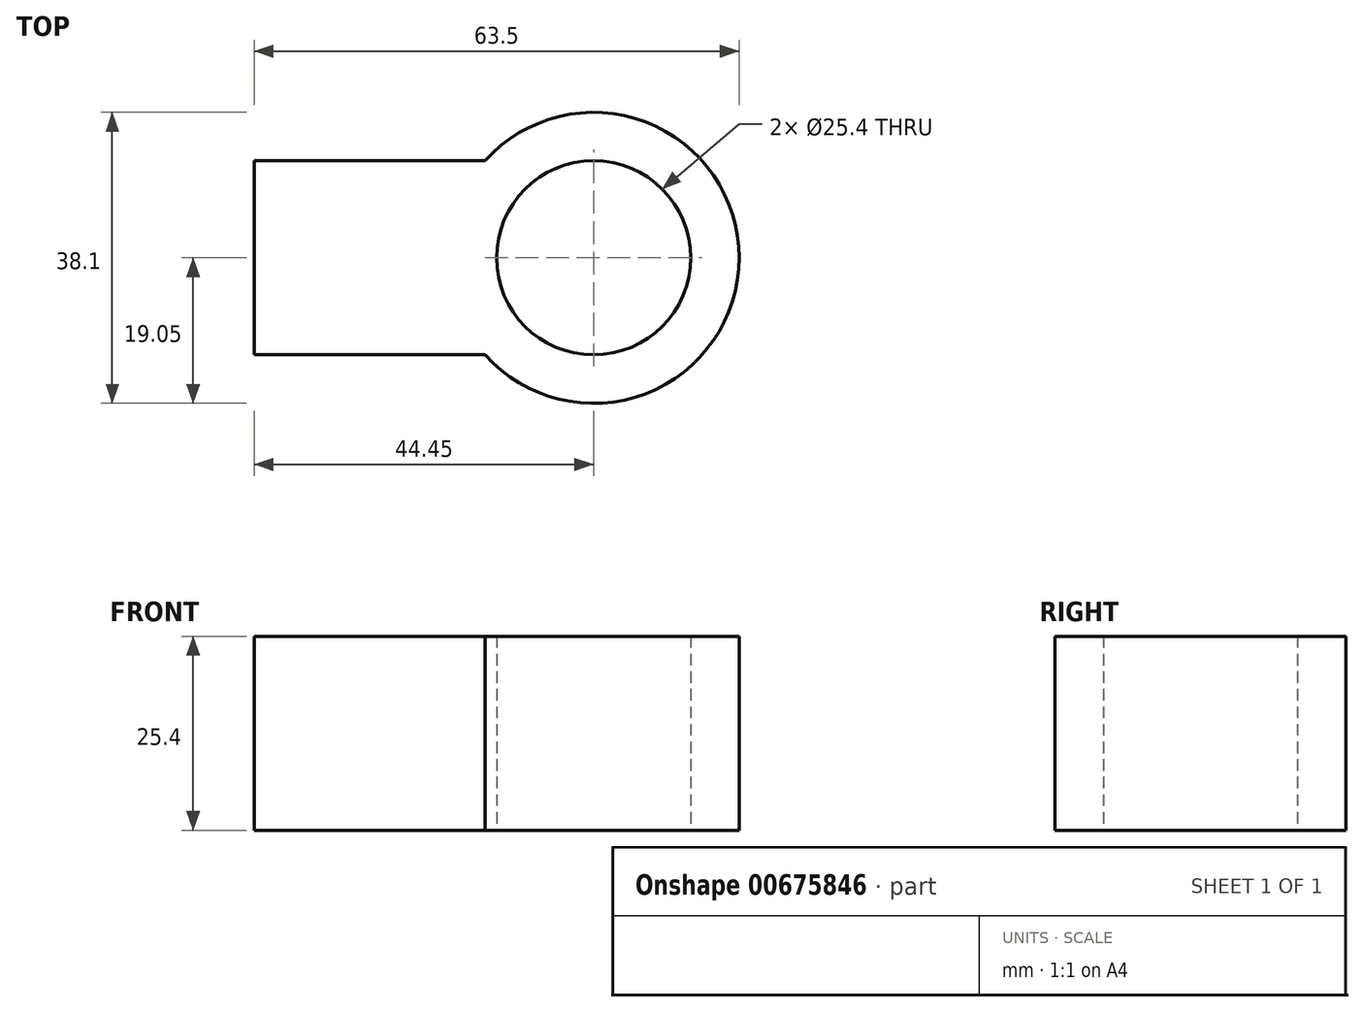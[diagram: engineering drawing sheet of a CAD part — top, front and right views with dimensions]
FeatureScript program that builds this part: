
annotation { "Feature Type Name" : "Feature", "Feature Type Description" : "" }
export const myFeature = defineFeature(function(context is Context, id is Id, definition is map)
    precondition{}
    {
        {
            var Q0;
            Q0=qCreatedBy(makeId("Top.planeOp"),FACE);
            var sketch = newSketch(context, id + "F0", { "sketchPlane" : qUnion([Q0])});
            skCircle(sketch, "E0", {"center": v(0, 0) * mm, "radius": 12.7 * mm});
            skCircle(sketch, "E1.0", {"center": v(0, 0) * mm, "radius": 19.05 * mm});
            skLineSegment(sketch, "E2.bottom", {"start": v(-44.45, -12.7) * mm, "end": v(6.35, -12.7) * mm});
            skLineSegment(sketch, "E2.top", {"start": v(-44.45, 12.7) * mm, "end": v(6.35, 12.7) * mm});
            skLineSegment(sketch, "E2.left", {"start": v(-44.45, 12.7) * mm, "end": v(-44.45, -12.7) * mm});
            skLineSegment(sketch, "E2.right", {"start": v(6.35, 12.7) * mm, "end": v(6.35, -12.7) * mm});
            skPoint(sketch, "E2.middle", {"position": v(-19.05, 0) * mm});
            skLineSegment(sketch, "E3", {"start": v(0, 0) * mm, "end": v(-19.05, 0) * mm});
            skSolve(sketch);
        }
        {
            var Q0;
            {var subQ0=sQuery(id+"F0.wireOp",EDGE,"E2.right");var subQ3=sQuery(id+"F0.wireOp",EDGE,"E0");var subQ9=makeQuery(id+"F0.imprint","INTERSECT",VERTEX,{"disambiguationData":[OD(0.0)],"derivedFrom":[subQ3,subQ0]});Q0=makeQuery(id+"F0.imprint","IMPRINT",FACE,{"disambiguationData":[TD([[makeQuery(id+"F0.imprint","IMPRINT",EDGE,{"disambiguationData":[TD([[subQ9,1.0]])],"derivedFrom":subQ3}),-1.0]])]});}
            var Q1;
            {var subQ0=sQuery(id+"F0.wireOp",EDGE,"E2.top");var subQ1=sQuery(id+"F0.wireOp",EDGE,"E0");var subQ2=makeQuery(id+"F0.imprint","INTERSECT",VERTEX,{"derivedFrom":[subQ1,subQ0]});Q1=makeQuery(id+"F0.imprint","IMPRINT",FACE,{"disambiguationData":[TD([[makeQuery(id+"F0.imprint","IMPRINT",EDGE,{"disambiguationData":[TD([[subQ2,1.0]])],"derivedFrom":subQ1}),-1.0]])]});}
            var Q2;
            {var subQ0=sQuery(id+"F0.wireOp",EDGE,"E2.bottom");var subQ1=sQuery(id+"F0.wireOp",EDGE,"E0");var subQ2=makeQuery(id+"F0.imprint","INTERSECT",VERTEX,{"derivedFrom":[subQ1,subQ0]});Q2=makeQuery(id+"F0.imprint","IMPRINT",FACE,{"disambiguationData":[TD([[makeQuery(id+"F0.imprint","IMPRINT",EDGE,{"disambiguationData":[TD([[subQ2,-1.0]])],"derivedFrom":subQ1}),-1.0]])]});}
            var Q3;
            {var subQ0=sQuery(id+"F0.wireOp",EDGE,"E3");var subQ1=sQuery(id+"F0.wireOp",EDGE,"E0");var subQ2=makeQuery(id+"F0.imprint","INTERSECT",VERTEX,{"derivedFrom":[subQ1,subQ0]});Q3=makeQuery(id+"F0.imprint","IMPRINT",FACE,{"disambiguationData":[TD([[makeQuery(id+"F0.imprint","IMPRINT",EDGE,{"disambiguationData":[TD([[subQ2,1.0]])],"derivedFrom":subQ1}),-1.0]])]});}
            var Q4;
            {var subQ0=sQuery(id+"F0.wireOp",EDGE,"E2.left");Q4=makeQuery(id+"F0.imprint","IMPRINT",FACE,{"disambiguationData":[TD([[makeQuery(id+"F0.imprint","IMPRINT",EDGE,{"derivedFrom":subQ0}),1.0]])]});}
            var Q5;
            {var subQ0=sQuery(id+"F0.wireOp",EDGE,"E3");var subQ1=sQuery(id+"F0.wireOp",EDGE,"E0");var subQ2=makeQuery(id+"F0.imprint","INTERSECT",VERTEX,{"derivedFrom":[subQ1,subQ0]});Q5=makeQuery(id+"F0.imprint","IMPRINT",FACE,{"disambiguationData":[TD([[makeQuery(id+"F0.imprint","IMPRINT",EDGE,{"disambiguationData":[TD([[subQ2,-1.0]])],"derivedFrom":subQ1}),-1.0]])]});}
            extrude(context, id + "F1", {"entities" : qUnion([Q0, Q1, Q2, Q3, Q4, Q5]), "depth" : 25.4 * mm, "offsetDistance" : 25.4 * mm});
        }
    });
